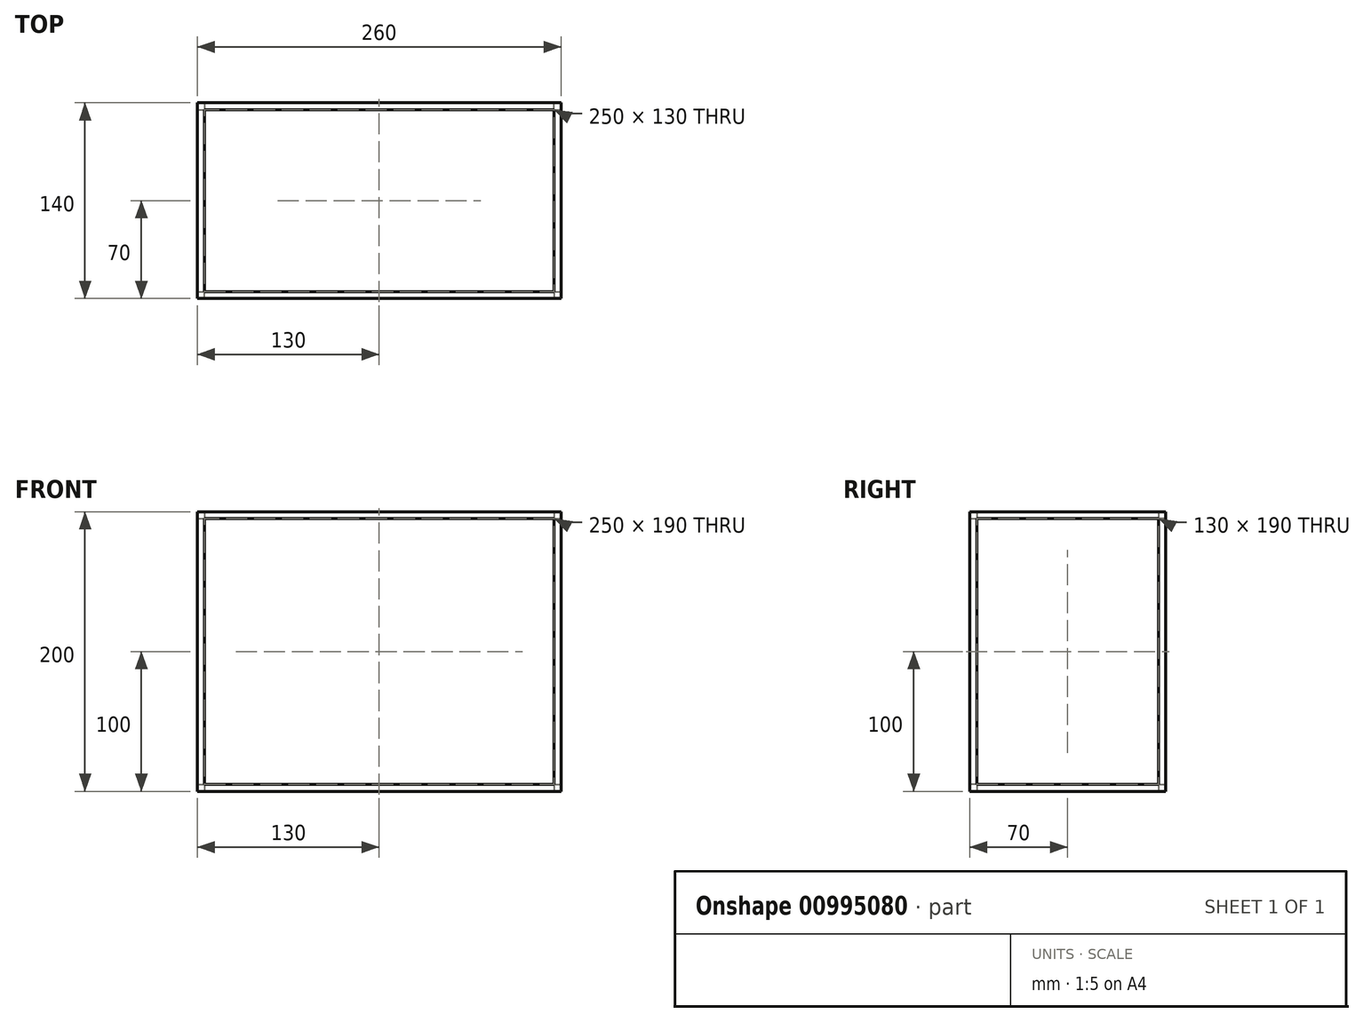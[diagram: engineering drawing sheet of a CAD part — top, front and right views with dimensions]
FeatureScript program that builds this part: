
annotation { "Feature Type Name" : "Feature", "Feature Type Description" : "" }
export const myFeature = defineFeature(function(context is Context, id is Id, definition is map)
    precondition{}
    {
        {
            var Q0;
            Q0=qCreatedBy(makeId("Top.planeOp"),FACE);
            var sketch = newSketch(context, id + "F0", { "sketchPlane" : qUnion([Q0])});
            skLineSegment(sketch, "E0.bottom", {"start": v(-132.65, 8.6) * mm, "end": v(117.35, 8.6) * mm});
            skLineSegment(sketch, "E0.top", {"start": v(-132.65, -121.4) * mm, "end": v(117.35, -121.4) * mm});
            skLineSegment(sketch, "E0.left", {"start": v(-132.65, 8.6) * mm, "end": v(-132.65, -121.4) * mm});
            skLineSegment(sketch, "E0.right", {"start": v(117.35, 8.6) * mm, "end": v(117.35, -121.4) * mm});
            skLineSegment(sketch, "E1.0", {"start": v(-137.65, 13.6) * mm, "end": v(-137.65, -126.4) * mm});
            skLineSegment(sketch, "E2.0", {"start": v(-137.65, 13.6) * mm, "end": v(122.35, 13.6) * mm});
            skLineSegment(sketch, "E3.0", {"start": v(122.35, 13.6) * mm, "end": v(122.35, -126.4) * mm});
            skLineSegment(sketch, "E4.0", {"start": v(-137.65, -126.4) * mm, "end": v(122.35, -126.4) * mm});
            skSolve(sketch);
        }
        {
            var Q0;
            Q0=makeQuery(id+"F0.imprint","IMPRINT",FACE,{"disambiguationData":[TD([[makeQuery(id+"F0.imprint","IMPRINT",EDGE,{"derivedFrom":sQuery(id+"F0.wireOp",EDGE,"E0.bottom")}),1.0]])]});
            extrude(context, id + "F1", {"entities" : qUnion([Q0]), "depth" : 5 * mm, "offsetDistance" : 25 * mm});
        }
        {
            var Q0;
            Q0=makeQuery(id+"F1.opExtrude","CAP_FACE",FACE,{"disambiguationData":[OSD([sQuery(id+"F0.wireOp",EDGE,"E0.bottom"),sQuery(id+"F0.wireOp",EDGE,"E0.top"),sQuery(id+"F0.wireOp",EDGE,"E0.left"),sQuery(id+"F0.wireOp",EDGE,"E0.right"),sQuery(id+"F0.wireOp",EDGE,"E1.0"),sQuery(id+"F0.wireOp",EDGE,"E2.0"),sQuery(id+"F0.wireOp",EDGE,"E3.0"),sQuery(id+"F0.wireOp",EDGE,"E4.0")])],"isStart":false});
            var sketch = newSketch(context, id + "F2", { "sketchPlane" : qUnion([Q0])});
            skLineSegment(sketch, "E5.bottom", {"start": v(-137.65, 13.6) * mm, "end": v(-132.65, 13.6) * mm});
            skLineSegment(sketch, "E5.top", {"start": v(-137.65, 8.6) * mm, "end": v(-132.65, 8.6) * mm});
            skLineSegment(sketch, "E5.left", {"start": v(-137.65, 13.6) * mm, "end": v(-137.65, 8.6) * mm});
            skLineSegment(sketch, "E5.right", {"start": v(-132.65, 13.6) * mm, "end": v(-132.65, 8.6) * mm});
            skLineSegment(sketch, "E6.bottom", {"start": v(-137.65, -126.4) * mm, "end": v(-132.65, -126.4) * mm});
            skLineSegment(sketch, "E6.top", {"start": v(-137.65, -121.4) * mm, "end": v(-132.65, -121.4) * mm});
            skLineSegment(sketch, "E6.left", {"start": v(-137.65, -126.4) * mm, "end": v(-137.65, -121.4) * mm});
            skLineSegment(sketch, "E6.right", {"start": v(-132.65, -126.4) * mm, "end": v(-132.65, -121.4) * mm});
            skLineSegment(sketch, "E7.bottom", {"start": v(117.35, -121.4) * mm, "end": v(122.35, -121.4) * mm});
            skLineSegment(sketch, "E7.top", {"start": v(117.35, -126.4) * mm, "end": v(122.35, -126.4) * mm});
            skLineSegment(sketch, "E7.left", {"start": v(117.35, -121.4) * mm, "end": v(117.35, -126.4) * mm});
            skLineSegment(sketch, "E7.right", {"start": v(122.35, -121.4) * mm, "end": v(122.35, -126.4) * mm});
            skLineSegment(sketch, "E8.bottom", {"start": v(117.35, 8.6) * mm, "end": v(122.35, 8.6) * mm});
            skLineSegment(sketch, "E8.top", {"start": v(117.35, 13.6) * mm, "end": v(122.35, 13.6) * mm});
            skLineSegment(sketch, "E8.left", {"start": v(117.35, 8.6) * mm, "end": v(117.35, 13.6) * mm});
            skLineSegment(sketch, "E8.right", {"start": v(122.35, 8.6) * mm, "end": v(122.35, 13.6) * mm});
            skSolve(sketch);
        }
        {
            var Q0;
            Q0 = qSketchRegion(id + "F2", true);
            extrude(context, id + "F3", {"entities" : qUnion([Q0]), "operationType" : NewBodyOperationType.ADD, "depth" : 190 * mm, "offsetDistance" : 25 * mm});
        }
        {
            var Q0;
            Q0=makeQuery(id+"F3.opExtrude","CAP_FACE",FACE,{"disambiguationData":[OSD([sQuery(id+"F2.wireOp",EDGE,"E5.bottom"),sQuery(id+"F2.wireOp",EDGE,"E5.top"),sQuery(id+"F2.wireOp",EDGE,"E5.left"),sQuery(id+"F2.wireOp",EDGE,"E5.right")])],"isStart":false});
            var sketch = newSketch(context, id + "F4", { "sketchPlane" : qUnion([Q0])});
            skLineSegment(sketch, "E9.bottom", {"start": v(-132.65, 8.6) * mm, "end": v(117.35, 8.6) * mm});
            skLineSegment(sketch, "E9.top", {"start": v(-132.65, -121.4) * mm, "end": v(117.35, -121.4) * mm});
            skLineSegment(sketch, "E9.left", {"start": v(-132.65, 8.6) * mm, "end": v(-132.65, -121.4) * mm});
            skLineSegment(sketch, "E9.right", {"start": v(117.35, 8.6) * mm, "end": v(117.35, -121.4) * mm});
            skLineSegment(sketch, "E10.0", {"start": v(-137.65, 13.6) * mm, "end": v(-137.65, -126.4) * mm});
            skLineSegment(sketch, "E11.0", {"start": v(-137.65, 13.6) * mm, "end": v(122.35, 13.6) * mm});
            skLineSegment(sketch, "E12.0", {"start": v(122.35, 13.6) * mm, "end": v(122.35, -126.4) * mm});
            skLineSegment(sketch, "E13.0", {"start": v(-137.65, -126.4) * mm, "end": v(122.35, -126.4) * mm});
            skLineSegment(sketch, "E14", {"start": v(-132.65, -116.66) * mm, "end": v(-21.65, -60.16) * mm});
            skLineSegment(sketch, "E15", {"start": v(113.43, 8.6) * mm, "end": v(117.35, 8.6) * mm});
            skLineSegment(sketch, "E16", {"start": v(117.35, 3.86) * mm, "end": v(6.35, -52.64) * mm});
            skLineSegment(sketch, "E17", {"start": v(-128.73, -121.4) * mm, "end": v(-132.65, -121.4) * mm});
            skLineSegment(sketch, "E18", {"start": v(-132.65, -116.66) * mm, "end": v(-132.65, -121.4) * mm});
            skLineSegment(sketch, "E19", {"start": v(117.35, 8.6) * mm, "end": v(117.35, 3.86) * mm});
            skPoint(sketch, "E20", {"position": v(-132.65, -56.4) * mm});
            skPoint(sketch, "E21", {"position": v(117.35, -56.4) * mm});
            skLineSegment(sketch, "E22", {"start": v(-132.65, -56.4) * mm, "end": v(-16.15, -56.4) * mm});
            skLineSegment(sketch, "E23.MirrorCS", {"start": v(117.35, -116.66) * mm, "end": v(6.35, -60.16) * mm});
            skLineSegment(sketch, "E24.MirrorCS", {"start": v(-132.65, 3.86) * mm, "end": v(-21.65, -52.64) * mm});
            skLineSegment(sketch, "E25.trimOffspring", {"start": v(6.85, -56.4) * mm, "end": v(117.35, -56.4) * mm});
            skLineSegment(sketch, "E26.trimOffspring", {"start": v(3.63, -47.3) * mm, "end": v(113.43, 8.6) * mm});
            skLineSegment(sketch, "E27.trimOffspring", {"start": v(3.63, -65.5) * mm, "end": v(113.43, -121.4) * mm});
            skLineSegment(sketch, "E28.trimOffspring", {"start": v(-18.93, -65.5) * mm, "end": v(-128.73, -121.4) * mm});
            skLineSegment(sketch, "E29.trimOffspring", {"start": v(-18.93, -47.3) * mm, "end": v(-128.73, 8.6) * mm});
            skCircle(sketch, "E30", {"center": v(-7.65, -56.4) * mm, "radius": 8.5 * mm});
            skArc(sketch, "E31", {"start": v(6.35, -60.16) * mm, "mid": v(6.85, -56.4) * mm, "end": v(6.35, -52.64) * mm});
            skArc(sketch, "E32.trimOffspring", {"start": v(-18.93, -65.5) * mm, "mid": v(-7.65, -70.9) * mm, "end": v(3.63, -65.5) * mm});
            skArc(sketch, "E33.trimOffspring", {"start": v(-21.65, -52.64) * mm, "mid": v(-22.15, -56.4) * mm, "end": v(-21.65, -60.16) * mm});
            skArc(sketch, "E34.trimOffspring", {"start": v(3.63, -47.3) * mm, "mid": v(-7.65, -41.9) * mm, "end": v(-18.93, -47.3) * mm});
            skSolve(sketch);
        }
        {
            var Q0;
            Q0=makeQuery(id+"F4.imprint","IMPRINT",FACE,{"disambiguationData":[TD([[makeQuery(id+"F4.imprint","IMPRINT",EDGE,{"derivedFrom":sQuery(id+"F4.wireOp",EDGE,"E9.bottom")}),1.0]])]});
            var Q1;
            {var subQ3=makeQuery(id+"F3.opExtrude","CAP_EDGE",EDGE,{"disambiguationData":[OSD([sQuery(id+"F2.wireOp",EDGE,"E5.top")])],"isStart":false});Q1=makeQuery(id+"F4.imprint","IMPRINT",FACE,{"disambiguationData":[TD([[makeQuery(id+"F4.imprint","IMPRINT",EDGE,{"derivedFrom":subQ3}),1.0]])]});}
            extrude(context, id + "F5", {"entities" : qUnion([Q0, Q1]), "operationType" : NewBodyOperationType.ADD, "depth" : 5 * mm, "offsetDistance" : 25 * mm});
        }
    });
